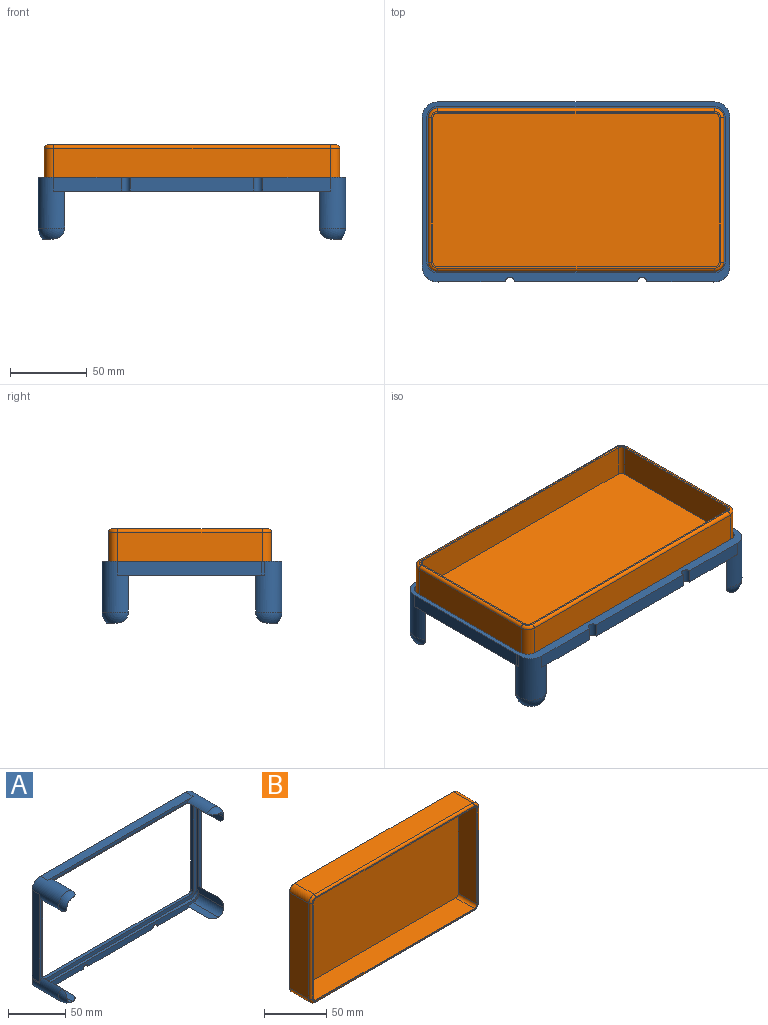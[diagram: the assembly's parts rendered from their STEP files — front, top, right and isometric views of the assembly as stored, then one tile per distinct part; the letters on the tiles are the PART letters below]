
ASSEMBLY  parts=2 mates=1
PART A: 53 faces, bbox 200x43x117 mm
  f0: plane 44x9mm, normal (0,0,-1), area 396mm2, adj f2,f3,f32,f52
  f1: plane 80x9mm, normal (0,0,-1), area 720mm2, adj f2,f3,f51,f52
  f2: plane 194x13mm, normal (0,-1,0), area 1064.2mm2, adj f0,f1,f4,f5,f6,f7,f16,f17
  f3: plane 200x117mm, normal (0,1,0), area 2375.7mm2, adj f0,f1,f7,f19,f20,f21,f22,f23
  f4: cylinder r=7mm len=7mm, axis (0,-1,0), area 33mm2, adj f2,f5,f16,f45
  f5: plane 180x3mm, normal (0,0,1), area 540mm2, adj f2,f4,f6,f45
  f6: cylinder r=7mm len=7mm, axis (0,-1,0), area 33mm2, adj f2,f5,f17,f45
  f7: cylinder r=10mm len=33mm, axis (0,-1,0), area 913.7mm2, adj f2,f3,f15,f16,f33,f34,f46,f47
  f8: sphere r=10mm, area 206.4mm2, adj f17,f32,f49,f50
  f9: sphere r=10mm, area 206.4mm2, adj f12,f17,f18,f29
  f10: sphere r=10mm, area 206.4mm2, adj f11,f16,f18,f27
  f11: cylinder r=7mm len=34.14mm, axis (0,-1,0), area 375.4mm2, adj f10,f16,f18,f45
  f12: cylinder r=7mm len=34.14mm, axis (0,-1,0), area 375.4mm2, adj f9,f17,f18,f45
  f13: plane 180x3mm, normal (0,-1,0), area 510.5mm2, adj f18,f27,f28,f29
  f14: plane 95.5x3mm, normal (0,-1,0), area 261.3mm2, adj f17,f29,f30,f31,f32
  f15: plane 95.5x3mm, normal (0,-1,0), area 261.3mm2, adj f7,f16,f26,f27,f34
  f16: plane 97x34.14mm, normal (-1,0,0), area 704.9mm2, adj f2,f4,f7,f10,f11,f15,f27,f45
  f17: plane 97x34.14mm, normal (1,0,0), area 704.9mm2, adj f2,f6,f8,f9,f12,f14,f29,f32
  f18: plane 180x34.14mm, normal (0,0,-1), area 962.9mm2, adj f9,f10,f11,f12,f13,f27,f29,f45
  f19: cylinder r=7mm len=7mm, axis (0,-1,0), area 33mm2, adj f3,f20,f35,f44
  f20: plane 94x3mm, normal (-1,0,0), area 282mm2, adj f3,f19,f21,f44
  f21: cylinder r=7mm len=7mm, axis (0,-1,0), area 33mm2, adj f3,f20,f22,f44
  f22: plane 180x3mm, normal (0,0,1), area 540mm2, adj f3,f21,f23,f44
  f23: cylinder r=7mm len=7mm, axis (0,-1,0), area 33mm2, adj f3,f22,f24,f44
  f24: plane 94x3mm, normal (1,0,0), area 282mm2, adj f3,f23,f25,f44
  f25: cylinder r=7mm len=7mm, axis (0,-1,0), area 33mm2, adj f3,f24,f35,f44
  f26: plane 94x9mm, normal (1,0,0), area 846mm2, adj f3,f15,f27,f34
  f27: cylinder r=10mm len=33mm, axis (0,-1,0), area 900.2mm2, adj f3,f10,f13,f15,f16,f18,f26,f28
  f28: plane 180x9mm, normal (0,0,1), area 1620mm2, adj f3,f13,f27,f29
  f29: cylinder r=10mm len=33mm, axis (0,-1,0), area 900.2mm2, adj f3,f9,f13,f14,f17,f18,f28,f30
  f30: plane 94x9mm, normal (-1,0,0), area 846mm2, adj f3,f14,f29,f31
  f31: cylinder r=10mm len=9mm, axis (0,-1,0), area 13.6mm2, adj f3,f14,f30,f32
  f32: cylinder r=10mm len=33mm, axis (0,-1,0), area 913.7mm2, adj f0,f2,f3,f8,f14,f17,f31,f49
  f33: plane 44x9mm, normal (0,0,-1), area 396mm2, adj f2,f3,f7,f51
  f34: cylinder r=10mm len=9mm, axis (0,-1,0), area 13.6mm2, adj f3,f7,f15,f26
  f35: plane 180x3mm, normal (0,0,-1), area 540mm2, adj f3,f19,f25,f44
  f36: plane 94x3mm, normal (1,0,0), area 282mm2, adj f37,f43,f44,f45
  f37: cylinder r=3mm len=3mm, axis (0,-1,0), area 14.1mm2, adj f36,f38,f44,f45
  f38: plane 180x3mm, normal (0,0,-1), area 540mm2, adj f37,f39,f44,f45
  f39: cylinder r=3mm len=3mm, axis (0,-1,0), area 14.1mm2, adj f38,f40,f44,f45
  f40: plane 94x3mm, normal (-1,0,0), area 282mm2, adj f39,f41,f44,f45
  f41: cylinder r=3mm len=3mm, axis (0,-1,0), area 14.1mm2, adj f40,f42,f44,f45
  f42: plane 180x3mm, normal (0,0,1), area 540mm2, adj f41,f43,f44,f45
  f43: cylinder r=3mm len=3mm, axis (0,-1,0), area 14.1mm2, adj f36,f42,f44,f45
  f44: plane 194x108mm, normal (0,1,0), area 2317.7mm2, adj f19,f20,f21,f22,f23,f24,f25,f35
  f45: plane 194x108mm, normal (0,-1,0), area 2317.7mm2, adj f4,f5,f6,f11,f12,f16,f17,f18
  f46: sphere r=10mm, area 206.4mm2, adj f7,f16,f47,f48
  f47: plane 31.14x7.14mm, normal (0,0,1), area 211.4mm2, adj f2,f7,f46,f48
  f48: cylinder r=7mm len=31.14mm, axis (0,1,0), area 342.4mm2, adj f2,f16,f46,f47
  f49: plane 31.14x7.14mm, normal (0,0,1), area 211.4mm2, adj f2,f8,f32,f50
  f50: cylinder r=7mm len=31.14mm, axis (0,1,0), area 342.4mm2, adj f2,f8,f17,f49
  f51: cylinder r=3mm len=9mm, axis (0,1,0), area 84.8mm2, adj f1,f2,f3,f33
  f52: cylinder r=3mm len=9mm, axis (0,1,0), area 84.8mm2, adj f0,f1,f2,f3
PART B: 27 faces, bbox 193x24x107 mm
  f0: cylinder r=6mm len=22mm, axis (0,-1,0), area 207.3mm2, adj f1,f7,f8,f20
  f1: plane 94x22mm, normal (-1,0,0), area 2068mm2, adj f0,f2,f8,f19
  f2: cylinder r=6mm len=22mm, axis (0,-1,0), area 207.3mm2, adj f1,f3,f8,f21
  f3: plane 180x22mm, normal (0,0,-1), area 3960mm2, adj f2,f4,f8,f23
  f4: cylinder r=6mm len=22mm, axis (0,-1,0), area 207.3mm2, adj f3,f5,f8,f25
  f5: plane 94x22mm, normal (1,0,0), area 2068mm2, adj f4,f6,f8,f26
  f6: cylinder r=6mm len=22mm, axis (0,-1,0), area 207.3mm2, adj f5,f7,f8,f24
  f7: plane 180x22mm, normal (0,0,1), area 3960mm2, adj f0,f6,f8,f22
  f8: plane 192x106mm, normal (0,1,0), area 20321.1mm2, adj f0,f1,f2,f3,f4,f5,f6,f7
  f9: plane 180x21mm, normal (0,0,-1), area 3780mm2, adj f10,f16,f17,f18
  f10: cylinder r=3mm len=21mm, axis (0,1,0), area 99mm2, adj f9,f11,f17,f18
  f11: plane 94x21mm, normal (-1,0,0), area 1974mm2, adj f10,f12,f17,f18
  f12: cylinder r=3mm len=21mm, axis (0,1,0), area 99mm2, adj f11,f13,f17,f18
  f13: plane 180x21mm, normal (0,0,1), area 3780mm2, adj f12,f14,f17,f18
  f14: cylinder r=3mm len=21mm, axis (0,1,0), area 99mm2, adj f13,f15,f17,f18
  f15: plane 94x21mm, normal (1,0,0), area 1974mm2, adj f14,f16,f17,f18
  f16: cylinder r=3mm len=21mm, axis (0,1,0), area 99mm2, adj f9,f15,f17,f18
  f17: plane 188x102mm, normal (0,-1,0), area 570mm2, adj f9,f10,f11,f12,f13,f14,f15,f16
  f18: plane 186x100mm, normal (0,-1,0), area 18592.3mm2, adj f9,f10,f11,f12,f13,f14,f15,f16
  f19: cylinder r=2mm len=94mm, axis (0,0,-1), area 295.3mm2, adj f1,f17,f20,f21
  f20: torus R=4mm, axis (0,-1,0), area 26mm2, adj f0,f17,f19,f22
  f21: torus R=4mm, axis (0,-1,0), area 26mm2, adj f2,f17,f19,f23
  f22: cylinder r=2mm len=180mm, axis (-1,0,0), area 565.5mm2, adj f7,f17,f20,f24
  f23: cylinder r=2mm len=180mm, axis (1,0,0), area 565.5mm2, adj f3,f17,f21,f25
  f24: torus R=4mm, axis (0,-1,0), area 26mm2, adj f6,f17,f22,f26
  f25: torus R=4mm, axis (0,-1,0), area 26mm2, adj f4,f17,f23,f26
  f26: cylinder r=2mm len=94mm, axis (0,0,1), area 295.3mm2, adj f5,f17,f24,f25
PLACE A rot(axis=(0,0.71,0.71),180deg) t=(-103.15,29.45,12.16)mm fixed
PLACE B rot(axis=(0,0.71,-0.71),180deg) t=(-103.15,30.78,18.16)mm
MATE slider B.f18 <-> A.f45  axis (0,0,1) through (-103.15,30.78,18.16)mm
